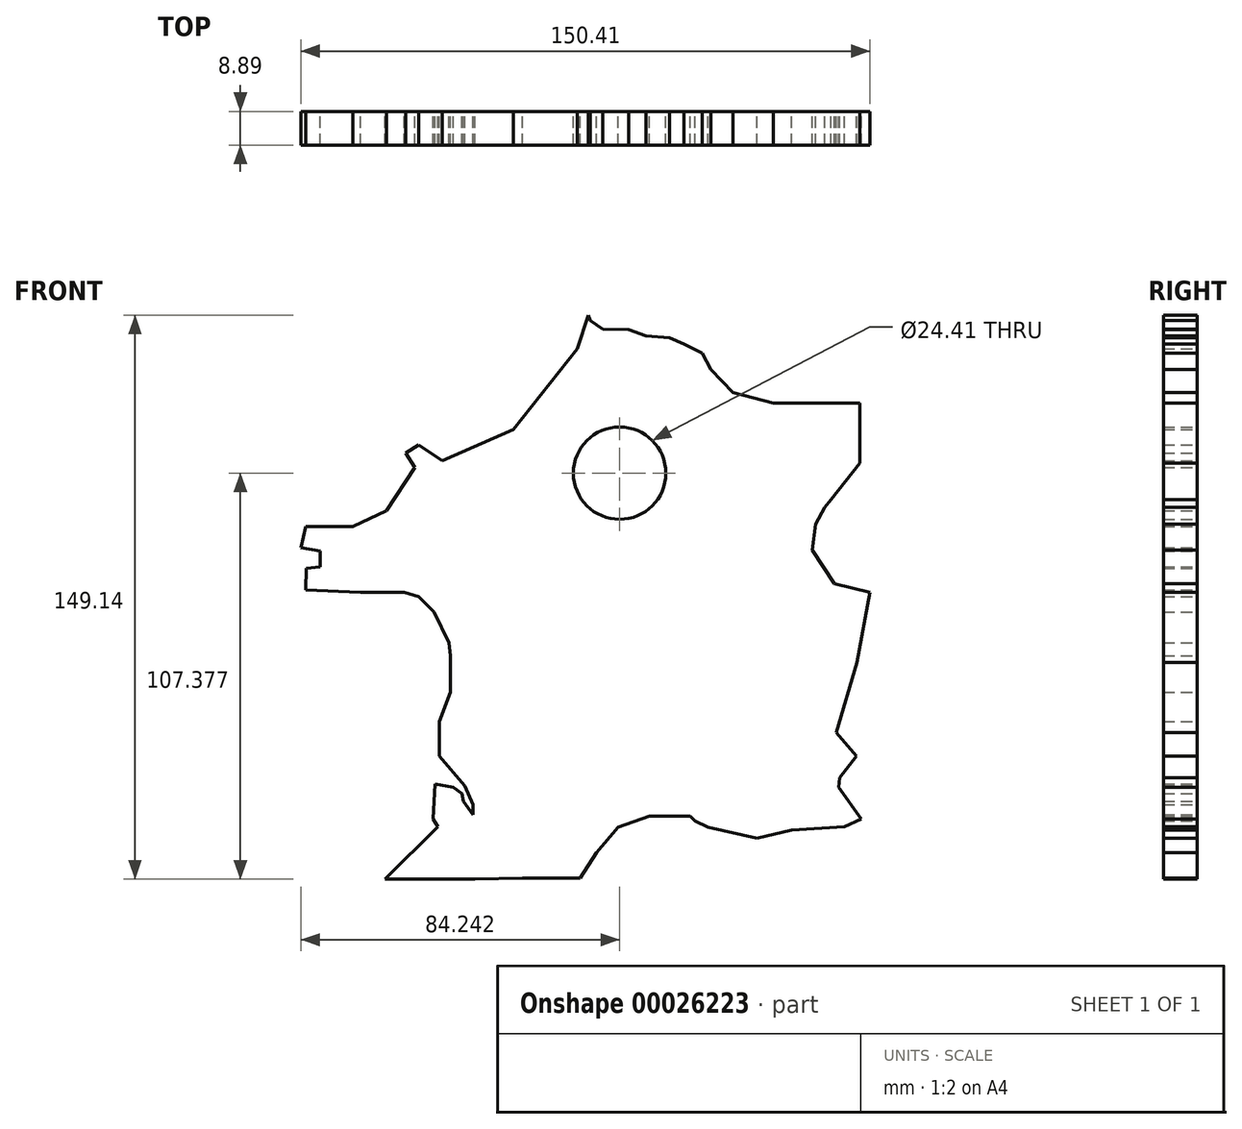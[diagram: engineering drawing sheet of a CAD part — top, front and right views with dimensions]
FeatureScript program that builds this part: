
annotation { "Feature Type Name" : "Feature", "Feature Type Description" : "" }
export const myFeature = defineFeature(function(context is Context, id is Id, definition is map)
    precondition{}
    {
        {
            var Q0;
            Q0=qCreatedBy(makeId("Front.planeOp"),FACE);
            var sketch = newSketch(context, id + "F0", { "sketchPlane" : qUnion([Q0])});
            skLineSegment(sketch, "E0", {"start": v(0, 64.42) * mm, "end": v(-16.85, 43.04) * mm});
            skLineSegment(sketch, "E1", {"start": v(-16.85, 43.04) * mm, "end": v(-35.7, 34.89) * mm});
            skLineSegment(sketch, "E2", {"start": v(-35.7, 34.89) * mm, "end": v(-41.86, 39.05) * mm});
            skLineSegment(sketch, "E3", {"start": v(-41.86, 39.05) * mm, "end": v(-45.3, 36.88) * mm});
            skLineSegment(sketch, "E4", {"start": v(-45.3, 36.88) * mm, "end": v(-42.9, 33.07) * mm});
            skLineSegment(sketch, "E5", {"start": v(-42.9, 33.07) * mm, "end": v(-50.38, 21.66) * mm});
            skLineSegment(sketch, "E6", {"start": v(-50.38, 21.66) * mm, "end": v(-59.26, 17.49) * mm});
            skLineSegment(sketch, "E7", {"start": v(-59.26, 17.49) * mm, "end": v(-71.76, 17.49) * mm});
            skLineSegment(sketch, "E8", {"start": v(-71.76, 17.49) * mm, "end": v(-73.03, 11.87) * mm});
            skLineSegment(sketch, "E9", {"start": v(-73.03, 11.87) * mm, "end": v(-67.96, 10.96) * mm});
            skLineSegment(sketch, "E10", {"start": v(-67.96, 10.96) * mm, "end": v(-67.96, 6.8) * mm});
            skLineSegment(sketch, "E11", {"start": v(-67.96, 6.8) * mm, "end": v(-71.58, 6.43) * mm});
            skLineSegment(sketch, "E12", {"start": v(-71.58, 6.43) * mm, "end": v(-71.76, 0.63) * mm});
            skLineSegment(sketch, "E13", {"start": v(-71.76, 0.63) * mm, "end": v(-57.27, 0) * mm});
            skLineSegment(sketch, "E14", {"start": v(-57.27, 0) * mm, "end": v(-45.67, 0) * mm});
            skLineSegment(sketch, "E15", {"start": v(-45.67, 0) * mm, "end": v(-41.86, -1.18) * mm});
            skLineSegment(sketch, "E16", {"start": v(-41.86, -1.18) * mm, "end": v(-37.88, -5.16) * mm});
            skLineSegment(sketch, "E17", {"start": v(-37.88, -5.16) * mm, "end": v(-33.89, -13.32) * mm});
            skLineSegment(sketch, "E18", {"start": v(-33.89, -13.32) * mm, "end": v(-33.53, -16.76) * mm});
            skLineSegment(sketch, "E19", {"start": v(-33.53, -16.76) * mm, "end": v(-33.53, -26.37) * mm});
            skLineSegment(sketch, "E20", {"start": v(-33.53, -26.37) * mm, "end": v(-36.43, -34.16) * mm});
            skLineSegment(sketch, "E21", {"start": v(-36.43, -34.16) * mm, "end": v(-36.43, -43.22) * mm});
            skLineSegment(sketch, "E22", {"start": v(-36.43, -43.22) * mm, "end": v(-29.72, -51.2) * mm});
            skLineSegment(sketch, "E23", {"start": v(-29.72, -51.2) * mm, "end": v(-27.55, -56.09) * mm});
            skLineSegment(sketch, "E24", {"start": v(-27.55, -56.09) * mm, "end": v(-27.55, -58.8) * mm});
            skLineSegment(sketch, "E25", {"start": v(-27.55, -58.8) * mm, "end": v(-30.08, -55.18) * mm});
            skLineSegment(sketch, "E26", {"start": v(-30.08, -55.18) * mm, "end": v(-30.45, -53.19) * mm});
            skLineSegment(sketch, "E27", {"start": v(-30.45, -53.19) * mm, "end": v(-32.8, -51.56) * mm});
            skLineSegment(sketch, "E28", {"start": v(-32.8, -51.56) * mm, "end": v(-37.51, -50.65) * mm});
            skLineSegment(sketch, "E29", {"start": v(-37.51, -50.65) * mm, "end": v(-38.06, -59.9) * mm});
            skLineSegment(sketch, "E30", {"start": v(-36.79, -61.89) * mm, "end": v(-50.74, -75.84) * mm});
            skLineSegment(sketch, "E31", {"start": v(-38.06, -59.9) * mm, "end": v(-36.79, -61.89) * mm});
            skLineSegment(sketch, "E32", {"start": v(-50.74, -75.84) * mm, "end": v(-27, -75.84) * mm});
            skLineSegment(sketch, "E33", {"start": v(-27, -75.84) * mm, "end": v(-14.5, -75.48) * mm});
            skLineSegment(sketch, "E34", {"start": v(-14.5, -75.48) * mm, "end": v(-6.52, -75.48) * mm});
            skLineSegment(sketch, "E35", {"start": v(-6.52, -75.48) * mm, "end": v(0.72, -75.48) * mm});
            skLineSegment(sketch, "E36", {"start": v(0.72, -75.48) * mm, "end": v(5.07, -68.77) * mm});
            skLineSegment(sketch, "E37", {"start": v(5.07, -68.77) * mm, "end": v(10.87, -62.07) * mm});
            skLineSegment(sketch, "E38", {"start": v(10.87, -62.07) * mm, "end": v(19.03, -59.17) * mm});
            skLineSegment(sketch, "E39", {"start": v(19.03, -59.17) * mm, "end": v(29.9, -59.17) * mm});
            skLineSegment(sketch, "E40", {"start": v(29.9, -59.17) * mm, "end": v(31.17, -60.44) * mm});
            skLineSegment(sketch, "E41", {"start": v(31.17, -60.44) * mm, "end": v(34.61, -62.07) * mm});
            skLineSegment(sketch, "E42", {"start": v(34.61, -62.07) * mm, "end": v(47.48, -64.97) * mm});
            skLineSegment(sketch, "E43", {"start": v(47.48, -64.97) * mm, "end": v(56.72, -62.8) * mm});
            skLineSegment(sketch, "E44", {"start": v(56.72, -62.8) * mm, "end": v(70.68, -61.89) * mm});
            skLineSegment(sketch, "E45", {"start": v(70.68, -61.89) * mm, "end": v(75.03, -59.9) * mm});
            skLineSegment(sketch, "E46", {"start": v(75.03, -59.9) * mm, "end": v(69.05, -51.56) * mm});
            skLineSegment(sketch, "E47", {"start": v(69.05, -51.56) * mm, "end": v(69.4, -49.02) * mm});
            skLineSegment(sketch, "E48", {"start": v(69.4, -49.02) * mm, "end": v(73.76, -43.22) * mm});
            skLineSegment(sketch, "E49", {"start": v(73.76, -43.22) * mm, "end": v(68.5, -37.06) * mm});
            skLineSegment(sketch, "E50", {"start": v(68.5, -37.06) * mm, "end": v(73.94, -18.58) * mm});
            skLineSegment(sketch, "E51", {"start": v(73.94, -18.58) * mm, "end": v(77.38, 0) * mm});
            skLineSegment(sketch, "E52", {"start": v(77.38, 0) * mm, "end": v(67.96, 2.27) * mm});
            skLineSegment(sketch, "E53", {"start": v(67.96, 2.27) * mm, "end": v(62.16, 11.15) * mm});
            skLineSegment(sketch, "E54", {"start": v(62.16, 11.15) * mm, "end": v(63.07, 18.03) * mm});
            skLineSegment(sketch, "E55", {"start": v(63.07, 18.03) * mm, "end": v(65.42, 22.56) * mm});
            skLineSegment(sketch, "E56", {"start": v(65.42, 22.56) * mm, "end": v(67.05, 24.56) * mm});
            skLineSegment(sketch, "E57", {"start": v(67.05, 24.56) * mm, "end": v(74.66, 34.16) * mm});
            skLineSegment(sketch, "E58", {"start": v(74.66, 34.16) * mm, "end": v(74.66, 50.1) * mm});
            skLineSegment(sketch, "E59", {"start": v(74.66, 50.1) * mm, "end": v(62.88, 50.1) * mm});
            skLineSegment(sketch, "E60", {"start": v(62.88, 50.1) * mm, "end": v(51.83, 50.1) * mm});
            skLineSegment(sketch, "E61", {"start": v(51.83, 50.1) * mm, "end": v(41.14, 52.83) * mm});
            skLineSegment(sketch, "E62", {"start": v(41.14, 52.83) * mm, "end": v(35.34, 58.99) * mm});
            skLineSegment(sketch, "E63", {"start": v(35.34, 58.99) * mm, "end": v(32.98, 63.34) * mm});
            skLineSegment(sketch, "E64", {"start": v(32.98, 63.34) * mm, "end": v(28.27, 65.7) * mm});
            skLineSegment(sketch, "E65", {"start": v(28.27, 65.7) * mm, "end": v(24.47, 67.32) * mm});
            skLineSegment(sketch, "E66", {"start": v(24.47, 67.32) * mm, "end": v(18.12, 67.87) * mm});
            skLineSegment(sketch, "E67", {"start": v(18.12, 67.87) * mm, "end": v(13.6, 69.5) * mm});
            skLineSegment(sketch, "E68", {"start": v(13.6, 69.5) * mm, "end": v(6.7, 69.68) * mm});
            skLineSegment(sketch, "E69", {"start": v(6.7, 69.68) * mm, "end": v(3.44, 71.85) * mm});
            skLineSegment(sketch, "E70", {"start": v(3.44, 71.85) * mm, "end": v(2.9, 73.3) * mm});
            skLineSegment(sketch, "E71", {"start": v(2.9, 73.3) * mm, "end": v(0, 64.42) * mm});
            skCircle(sketch, "E72", {"center": v(11.21, 31.54) * mm, "radius": 12.2 * mm});
            skSolve(sketch);
        }
        {
            var Q0;
            Q0 = qSketchRegion(id + "F0", true);
            extrude(context, id + "F1", {"entities" : qUnion([Q0]), "depth" : 8.9 * mm});
        }
    });
